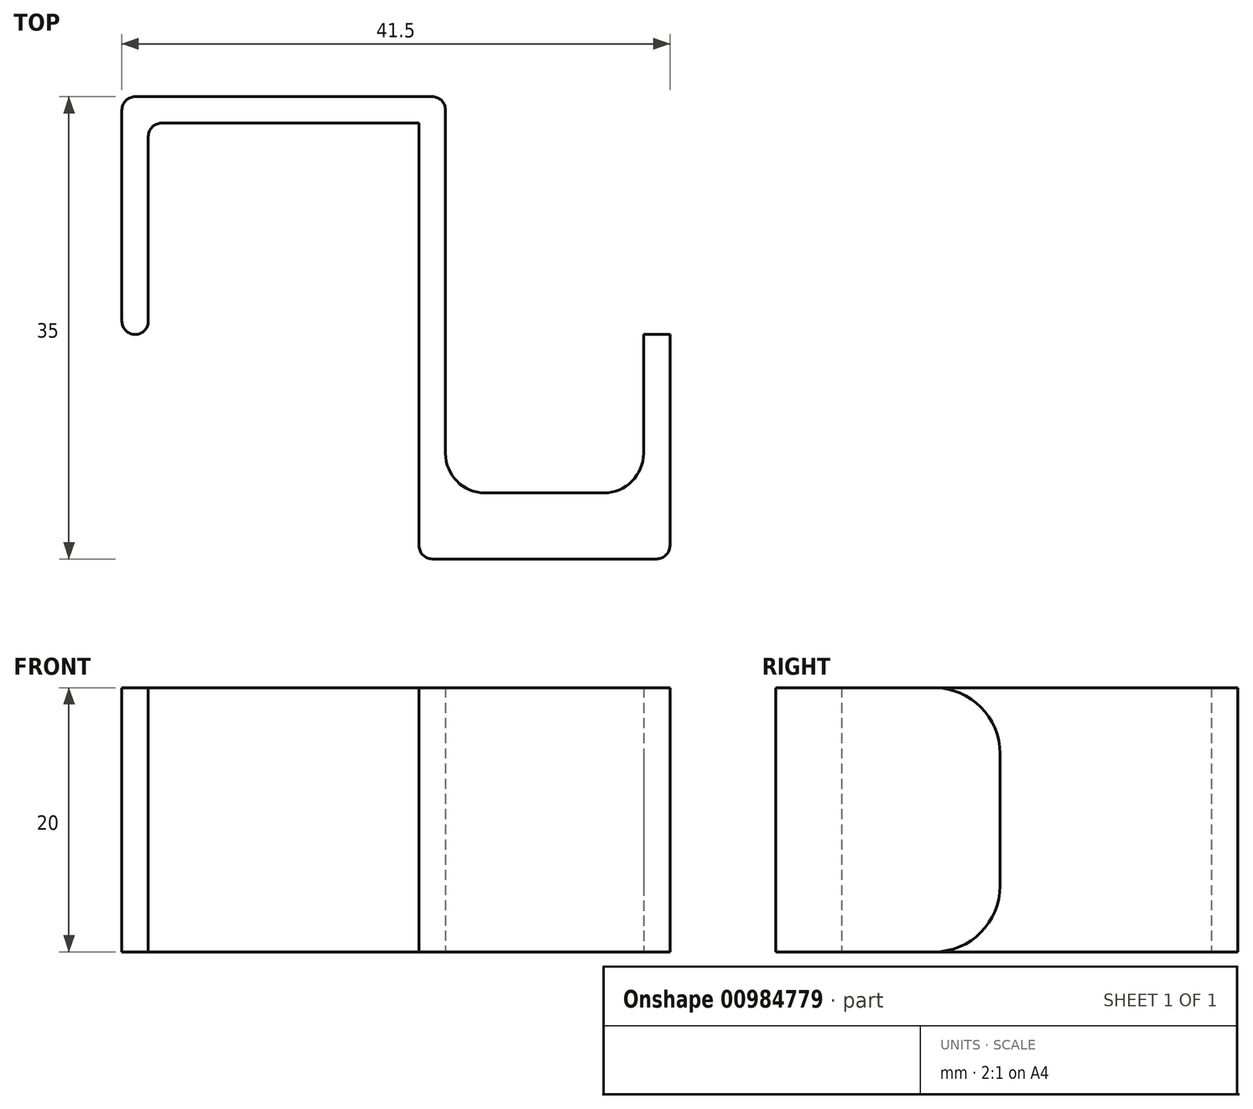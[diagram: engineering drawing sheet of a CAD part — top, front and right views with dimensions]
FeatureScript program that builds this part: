
annotation { "Feature Type Name" : "Feature", "Feature Type Description" : "" }
export const myFeature = defineFeature(function(context is Context, id is Id, definition is map)
    precondition{}
    {
        {
            var Q0;
            Q0=qCreatedBy(makeId("Top.planeOp"),FACE);
            var sketch = newSketch(context, id + "F0", { "sketchPlane" : qUnion([Q0])});
            skLineSegment(sketch, "E0", {"start": v(0, 0) * mm, "end": v(2, 0) * mm});
            skLineSegment(sketch, "E1", {"start": v(0, 0) * mm, "end": v(0, 18) * mm});
            skLineSegment(sketch, "E2", {"start": v(0, 18) * mm, "end": v(24.5, 18) * mm});
            skLineSegment(sketch, "E3", {"start": v(24.5, 18) * mm, "end": v(24.5, -12) * mm});
            skLineSegment(sketch, "E4", {"start": v(24.5, -12) * mm, "end": v(39.5, -12) * mm});
            skLineSegment(sketch, "E5", {"start": v(39.5, -12) * mm, "end": v(39.5, 0) * mm});
            skLineSegment(sketch, "E6", {"start": v(39.5, 0) * mm, "end": v(41.5, 0) * mm});
            skLineSegment(sketch, "E7", {"start": v(41.5, 0) * mm, "end": v(41.5, -17) * mm});
            skLineSegment(sketch, "E8", {"start": v(41.5, -17) * mm, "end": v(22.5, -17) * mm});
            skLineSegment(sketch, "E9", {"start": v(22.5, -17) * mm, "end": v(22.5, 16) * mm});
            skLineSegment(sketch, "E10", {"start": v(22.5, 16) * mm, "end": v(2, 16) * mm});
            skLineSegment(sketch, "E11", {"start": v(2, 16) * mm, "end": v(2, 0) * mm});
            skLineSegment(sketch, "E12", {"start": v(2, 0) * mm, "end": v(0, 0) * mm});
            skSolve(sketch);
        }
        {
            var Q0;
            Q0=makeQuery(id+"F0.imprint","IMPRINT",FACE,{"disambiguationData":[TD([[makeQuery(id+"F0.imprint","IMPRINT",EDGE,{"derivedFrom":sQuery(id+"F0.wireOp",EDGE,"E1")}),-1.0]])]});
            extrude(context, id + "F1", {"entities" : qUnion([Q0]), "depth" : 20 * mm, "offsetDistance" : 25 * mm});
        }
        {
            var Q0;
            Q0=makeQuery(id+"F1.opExtrude","CAP_EDGE",EDGE,{"disambiguationData":[OSD([sQuery(id+"F0.wireOp",EDGE,"E6")])],"isStart":false});
            var Q1;
            Q1=makeQuery(id+"F1.opExtrude","CAP_EDGE",EDGE,{"disambiguationData":[OSD([sQuery(id+"F0.wireOp",EDGE,"E6")])],"isStart":true});
            fillet(context, id + "F2", {"entities" : qUnion([Q0, Q1]), "radius" : 5 * mm, "tangentPropagation" : true, "allowEdgeOverflow" : false});
        }
        {
            var Q0;
            Q0=makeQuery(id+"F1.opExtrude","SWEPT_EDGE",EDGE,{"disambiguationData":[OSD([sQuery(id+"F0.wireOp",EDGE,"E1"),sQuery(id+"F0.wireOp",EDGE,"E2")])]});
            var Q1;
            Q1=makeQuery(id+"F1.opExtrude","SWEPT_EDGE",EDGE,{"disambiguationData":[OSD([sQuery(id+"F0.wireOp",EDGE,"E2"),sQuery(id+"F0.wireOp",EDGE,"E3")])]});
            var Q2;
            Q2=makeQuery(id+"F1.opExtrude","SWEPT_EDGE",EDGE,{"disambiguationData":[OSD([sQuery(id+"F0.wireOp",EDGE,"E11"),sQuery(id+"F0.wireOp",EDGE,"E12")])]});
            var Q3;
            Q3=makeQuery(id+"F1.opExtrude","SWEPT_EDGE",EDGE,{"disambiguationData":[OSD([sQuery(id+"F0.wireOp",EDGE,"E8"),sQuery(id+"F0.wireOp",EDGE,"E9")])]});
            var Q4;
            Q4=makeQuery(id+"F1.opExtrude","SWEPT_EDGE",EDGE,{"disambiguationData":[OSD([sQuery(id+"F0.wireOp",EDGE,"E7"),sQuery(id+"F0.wireOp",EDGE,"E8")])]});
            var Q5;
            Q5=makeQuery(id+"F1.opExtrude","SWEPT_EDGE",EDGE,{"disambiguationData":[OSD([sQuery(id+"F0.wireOp",EDGE,"E1"),sQuery(id+"F0.wireOp",EDGE,"E12")])]});
            fillet(context, id + "F3", {"entities" : qUnion([Q0, Q1, Q2, Q3, Q4, Q5]), "radius" : 1 * mm, "tangentPropagation" : true, "allowEdgeOverflow" : false});
        }
        {
            var Q0;
            Q0=makeQuery(id+"F1.opExtrude","SWEPT_EDGE",EDGE,{"disambiguationData":[OSD([sQuery(id+"F0.wireOp",EDGE,"E3"),sQuery(id+"F0.wireOp",EDGE,"E4")])]});
            var Q1;
            Q1=makeQuery(id+"F1.opExtrude","SWEPT_EDGE",EDGE,{"disambiguationData":[OSD([sQuery(id+"F0.wireOp",EDGE,"E4"),sQuery(id+"F0.wireOp",EDGE,"E5")])]});
            fillet(context, id + "F4", {"entities" : qUnion([Q0, Q1]), "radius" : 3 * mm, "tangentPropagation" : true, "allowEdgeOverflow" : false});
        }
    });
